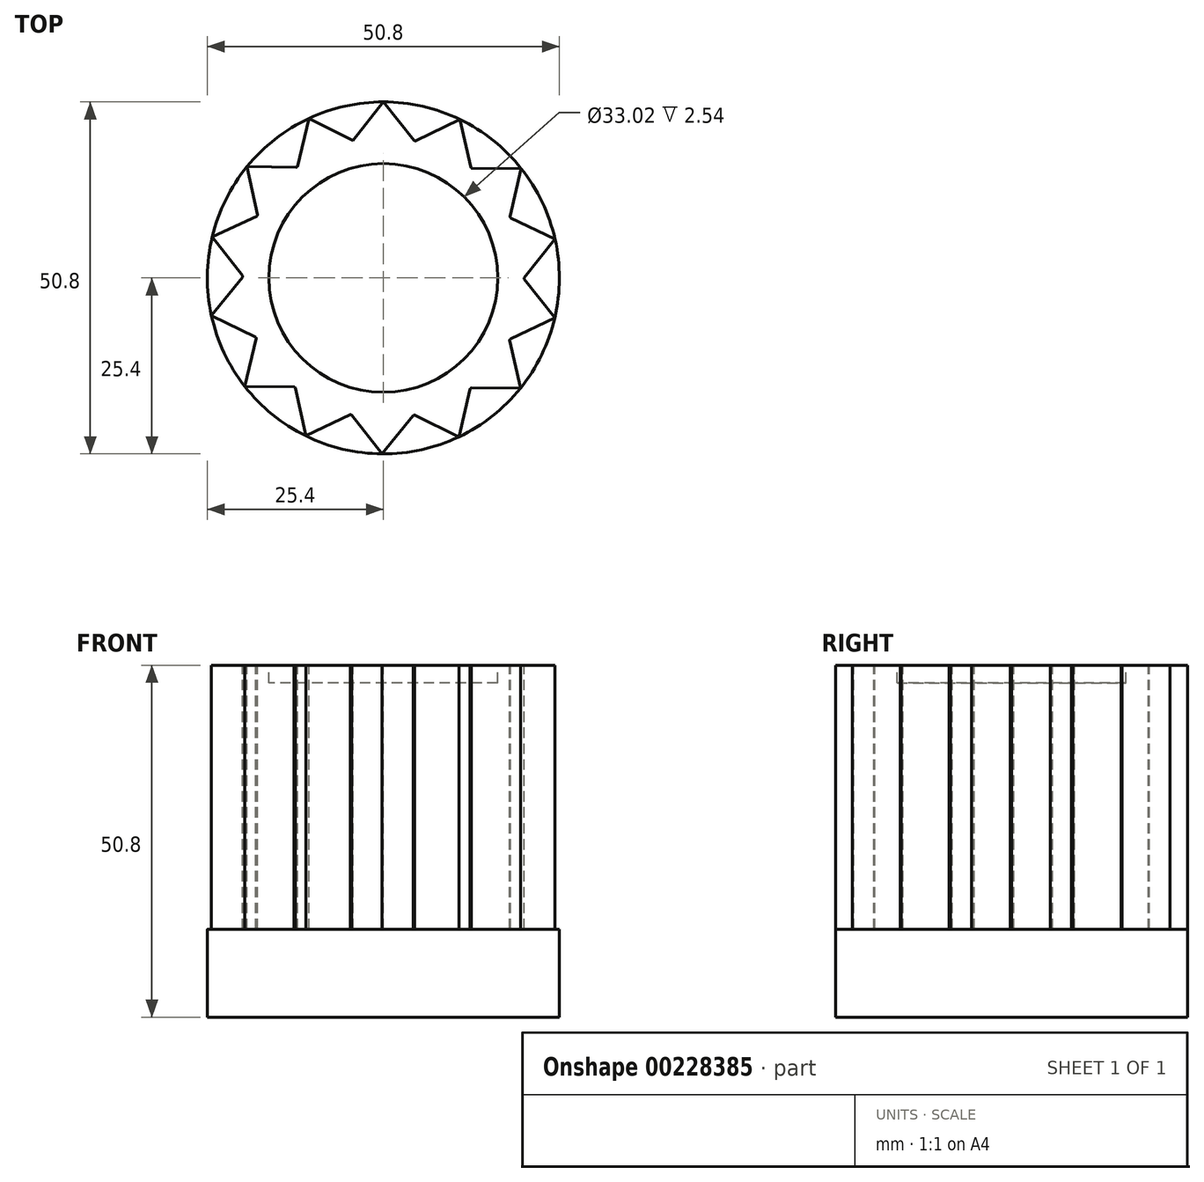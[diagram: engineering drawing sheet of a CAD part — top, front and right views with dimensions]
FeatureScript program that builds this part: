
annotation { "Feature Type Name" : "Feature", "Feature Type Description" : "" }
export const myFeature = defineFeature(function(context is Context, id is Id, definition is map)
    precondition{}
    {
        {
            var Q0;
            Q0=qCreatedBy(makeId("Top.planeOp"),FACE);
            var sketch = newSketch(context, id + "F0", { "sketchPlane" : qUnion([Q0])});
            skCircle(sketch, "E0", {"center": v(0, 0) * mm, "radius": 25.4 * mm});
            skSolve(sketch);
        }
        {
            var Q0;
            Q0 = qSketchRegion(id + "F0", true);
            extrude(context, id + "F1", {"entities" : qUnion([Q0]), "endBound" : BoundingType.SYMMETRIC, "depth" : 50.8 * mm});
        }
        {
            var Q0;
            Q0=makeQuery(id+"F1.opExtrude","CAP_FACE",FACE,{"disambiguationData":[OSD([sQuery(id+"F0.wireOp",EDGE,"E0")])],"isStart":false});
            var sketch = newSketch(context, id + "F2", { "sketchPlane" : qUnion([Q0])});
            skCircle(sketch, "E1.0", {"center": v(0, 0) * mm, "radius": 20.32 * mm});
            skLineSegment(sketch, "E2", {"start": v(0, 25.4) * mm, "end": v(-4.43, 19.83) * mm});
            skLineSegment(sketch, "E3", {"start": v(0, 25.4) * mm, "end": v(4.43, 19.83) * mm});
            skLineSegment(sketch, "E4.1.0", {"start": v(11.04, 22.87) * mm, "end": v(12.6, 15.94) * mm});
            skLineSegment(sketch, "E4.1.1", {"start": v(11.04, 22.87) * mm, "end": v(4.64, 19.78) * mm});
            skLineSegment(sketch, "E4.2.0", {"start": v(19.89, 15.8) * mm, "end": v(18.28, 8.87) * mm});
            skLineSegment(sketch, "E4.2.1", {"start": v(19.89, 15.8) * mm, "end": v(12.78, 15.8) * mm});
            skLineSegment(sketch, "E4.3.0", {"start": v(24.78, 5.58) * mm, "end": v(20.32, 0.04) * mm});
            skLineSegment(sketch, "E4.3.1", {"start": v(24.78, 5.58) * mm, "end": v(18.38, 8.67) * mm});
            skLineSegment(sketch, "E4.4.0", {"start": v(24.74, -5.75) * mm, "end": v(18.32, -8.8) * mm});
            skLineSegment(sketch, "E4.4.1", {"start": v(24.74, -5.75) * mm, "end": v(20.32, -0.18) * mm});
            skLineSegment(sketch, "E4.5.0", {"start": v(19.78, -15.93) * mm, "end": v(12.67, -15.89) * mm});
            skLineSegment(sketch, "E4.5.1", {"start": v(19.78, -15.93) * mm, "end": v(18.22, -9) * mm});
            skLineSegment(sketch, "E4.6.0", {"start": v(10.89, -22.95) * mm, "end": v(4.5, -19.81) * mm});
            skLineSegment(sketch, "E4.6.1", {"start": v(10.89, -22.95) * mm, "end": v(12.5, -16.02) * mm});
            skLineSegment(sketch, "E4.7.0", {"start": v(-0.17, -25.4) * mm, "end": v(-4.56, -19.8) * mm});
            skLineSegment(sketch, "E4.7.1", {"start": v(-0.17, -25.4) * mm, "end": v(4.3, -19.86) * mm});
            skLineSegment(sketch, "E4.8.0", {"start": v(-11.2, -22.8) * mm, "end": v(-12.71, -15.85) * mm});
            skLineSegment(sketch, "E4.8.1", {"start": v(-11.2, -22.8) * mm, "end": v(-4.77, -19.75) * mm});
            skLineSegment(sketch, "E4.9.0", {"start": v(-20, -15.66) * mm, "end": v(-18.34, -8.75) * mm});
            skLineSegment(sketch, "E4.9.1", {"start": v(-20, -15.66) * mm, "end": v(-12.88, -15.71) * mm});
            skLineSegment(sketch, "E4.10.0", {"start": v(-24.82, -5.41) * mm, "end": v(-20.32, 0.1) * mm});
            skLineSegment(sketch, "E4.10.1", {"start": v(-24.82, -5.41) * mm, "end": v(-18.43, -8.55) * mm});
            skLineSegment(sketch, "E4.11.0", {"start": v(-24.7, 5.91) * mm, "end": v(-18.26, 8.92) * mm});
            skLineSegment(sketch, "E4.11.1", {"start": v(-24.7, 5.91) * mm, "end": v(-20.32, 0.31) * mm});
            skLineSegment(sketch, "E4.12.0", {"start": v(-19.67, 16.06) * mm, "end": v(-12.56, 15.97) * mm});
            skLineSegment(sketch, "E4.12.1", {"start": v(-19.67, 16.06) * mm, "end": v(-18.16, 9.12) * mm});
            skLineSegment(sketch, "E4.13.0", {"start": v(-10.73, 23.02) * mm, "end": v(-4.37, 19.84) * mm});
            skLineSegment(sketch, "E4.13.1", {"start": v(-10.73, 23.02) * mm, "end": v(-12.4, 16.1) * mm});
            skLineSegment(sketch, "E4.anchor1", {"start": v(0, 0) * mm, "end": v(4.43, 19.83) * mm, "construction": true});
            skLineSegment(sketch, "E4.anchor2", {"start": v(0, 0) * mm, "end": v(-4.37, 19.84) * mm, "construction": true});
            skSolve(sketch);
        }
        {
            var Q0;
            {var subQ0=sQuery(id+"F2.wireOp",EDGE,"E2");var subQ3=sQuery(id+"F2.wireOp",EDGE,"E4.13.0");var subQ4=makeQuery(id+"F2.imprint","INTERSECT",VERTEX,{"derivedFrom":[subQ0,subQ3]});Q0=makeQuery(id+"F2.imprint","IMPRINT",FACE,{"disambiguationData":[TD([[makeQuery(id+"F2.imprint","IMPRINT",EDGE,{"disambiguationData":[TD([[subQ4,1.0]])],"derivedFrom":subQ0}),-1.0]])]});}
            var Q1;
            {var subQ0=sQuery(id+"F2.wireOp",EDGE,"E3");Q1=makeQuery(id+"F2.imprint","IMPRINT",FACE,{"disambiguationData":[TD([[makeQuery(id+"F2.imprint","IMPRINT",EDGE,{"derivedFrom":subQ0}),1.0]])]});}
            var Q2;
            {var subQ0=sQuery(id+"F2.wireOp",EDGE,"E4.1.0");Q2=makeQuery(id+"F2.imprint","IMPRINT",FACE,{"disambiguationData":[TD([[makeQuery(id+"F2.imprint","IMPRINT",EDGE,{"derivedFrom":subQ0}),1.0]])]});}
            var Q3;
            {var subQ0=sQuery(id+"F2.wireOp",EDGE,"E4.2.0");Q3=makeQuery(id+"F2.imprint","IMPRINT",FACE,{"disambiguationData":[TD([[makeQuery(id+"F2.imprint","IMPRINT",EDGE,{"derivedFrom":subQ0}),1.0]])]});}
            var Q4;
            {var subQ0=sQuery(id+"F2.wireOp",EDGE,"E4.3.0");Q4=makeQuery(id+"F2.imprint","IMPRINT",FACE,{"disambiguationData":[TD([[makeQuery(id+"F2.imprint","IMPRINT",EDGE,{"derivedFrom":subQ0}),1.0]])]});}
            var Q5;
            {var subQ0=sQuery(id+"F2.wireOp",EDGE,"E4.4.0");Q5=makeQuery(id+"F2.imprint","IMPRINT",FACE,{"disambiguationData":[TD([[makeQuery(id+"F2.imprint","IMPRINT",EDGE,{"derivedFrom":subQ0}),1.0]])]});}
            var Q6;
            {var subQ0=sQuery(id+"F2.wireOp",EDGE,"E4.5.0");Q6=makeQuery(id+"F2.imprint","IMPRINT",FACE,{"disambiguationData":[TD([[makeQuery(id+"F2.imprint","IMPRINT",EDGE,{"derivedFrom":subQ0}),1.0]])]});}
            var Q7;
            {var subQ0=sQuery(id+"F2.wireOp",EDGE,"E4.6.0");Q7=makeQuery(id+"F2.imprint","IMPRINT",FACE,{"disambiguationData":[TD([[makeQuery(id+"F2.imprint","IMPRINT",EDGE,{"derivedFrom":subQ0}),1.0]])]});}
            var Q8;
            {var subQ0=sQuery(id+"F2.wireOp",EDGE,"E4.7.0");Q8=makeQuery(id+"F2.imprint","IMPRINT",FACE,{"disambiguationData":[TD([[makeQuery(id+"F2.imprint","IMPRINT",EDGE,{"derivedFrom":subQ0}),1.0]])]});}
            var Q9;
            {var subQ0=sQuery(id+"F2.wireOp",EDGE,"E4.8.0");Q9=makeQuery(id+"F2.imprint","IMPRINT",FACE,{"disambiguationData":[TD([[makeQuery(id+"F2.imprint","IMPRINT",EDGE,{"derivedFrom":subQ0}),1.0]])]});}
            var Q10;
            {var subQ0=sQuery(id+"F2.wireOp",EDGE,"E4.9.0");Q10=makeQuery(id+"F2.imprint","IMPRINT",FACE,{"disambiguationData":[TD([[makeQuery(id+"F2.imprint","IMPRINT",EDGE,{"derivedFrom":subQ0}),1.0]])]});}
            var Q11;
            {var subQ0=sQuery(id+"F2.wireOp",EDGE,"E4.10.0");Q11=makeQuery(id+"F2.imprint","IMPRINT",FACE,{"disambiguationData":[TD([[makeQuery(id+"F2.imprint","IMPRINT",EDGE,{"derivedFrom":subQ0}),1.0]])]});}
            var Q12;
            {var subQ0=sQuery(id+"F2.wireOp",EDGE,"E4.11.0");Q12=makeQuery(id+"F2.imprint","IMPRINT",FACE,{"disambiguationData":[TD([[makeQuery(id+"F2.imprint","IMPRINT",EDGE,{"derivedFrom":subQ0}),1.0]])]});}
            var Q13;
            {var subQ0=sQuery(id+"F2.wireOp",EDGE,"E4.12.0");Q13=makeQuery(id+"F2.imprint","IMPRINT",FACE,{"disambiguationData":[TD([[makeQuery(id+"F2.imprint","IMPRINT",EDGE,{"derivedFrom":subQ0}),1.0]])]});}
            extrude(context, id + "F3", {"entities" : qUnion([Q0, Q1, Q2, Q3, Q4, Q5, Q6, Q7, Q8, Q9, Q10, Q11, Q12, Q13]), "operationType" : NewBodyOperationType.REMOVE, "oppositeDirection" : true, "depth" : 38.1 * mm});
        }
        {
            var Q0;
            Q0=makeQuery(id+"F1.opExtrude","CAP_FACE",FACE,{"disambiguationData":[OSD([sQuery(id+"F0.wireOp",EDGE,"E0")])],"isStart":false});
            var sketch = newSketch(context, id + "F4", { "sketchPlane" : qUnion([Q0])});
            skCircle(sketch, "E5", {"center": v(0, 0) * mm, "radius": 16.51 * mm});
            skSolve(sketch);
        }
        {
            var Q0;
            Q0=makeQuery(id+"F4.imprint","IMPRINT",FACE,{"disambiguationData":[TD([[makeQuery(id+"F4.imprint","IMPRINT",EDGE,{"derivedFrom":sQuery(id+"F4.wireOp",EDGE,"E5")}),1.0]])]});
            extrude(context, id + "F5", {"entities" : qUnion([Q0]), "operationType" : NewBodyOperationType.REMOVE, "oppositeDirection" : true, "depth" : 2.54 * mm});
        }
    });
